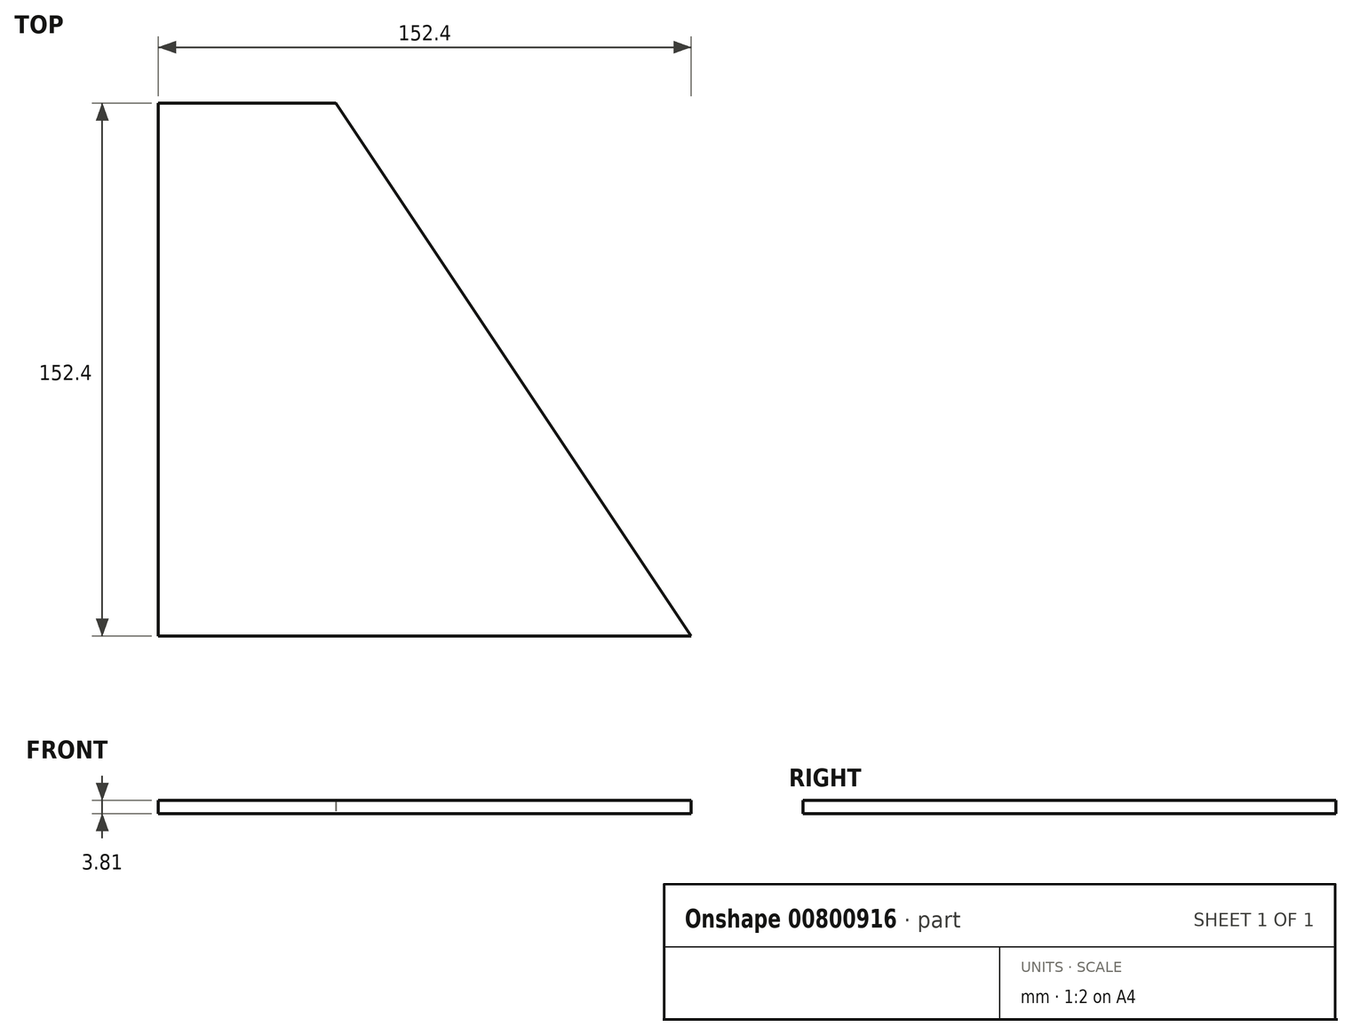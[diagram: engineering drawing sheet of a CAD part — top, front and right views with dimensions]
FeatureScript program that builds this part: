
annotation { "Feature Type Name" : "Feature", "Feature Type Description" : "" }
export const myFeature = defineFeature(function(context is Context, id is Id, definition is map)
    precondition{}
    {
        {
            var Q0;
            Q0=qCreatedBy(makeId("Top.planeOp"),FACE);
            var sketch = newSketch(context, id + "F0", { "sketchPlane" : qUnion([Q0])});
            skLineSegment(sketch, "E0.bottom", {"start": v(-98.53, -54.62) * mm, "end": v(53.87, -54.62) * mm});
            skLineSegment(sketch, "E0.left", {"start": v(-98.53, -54.62) * mm, "end": v(-98.53, 97.78) * mm});
            skLineSegment(sketch, "E1", {"start": v(-98.53, 97.78) * mm, "end": v(-47.73, 97.78) * mm});
            skLineSegment(sketch, "E2", {"start": v(-47.73, 97.78) * mm, "end": v(53.87, -54.62) * mm});
            skSolve(sketch);
        }
        {
            var Q0;
            Q0=makeQuery(id+"F0.imprint","IMPRINT",FACE,{"disambiguationData":[TD([[makeQuery(id+"F0.imprint","IMPRINT",EDGE,{"derivedFrom":sQuery(id+"F0.wireOp",EDGE,"E0.bottom")}),1.0]])]});
            extrude(context, id + "F1", {"entities" : qUnion([Q0]), "depth" : 3.8 * mm, "offsetDistance" : 25.4 * mm});
        }
    });
